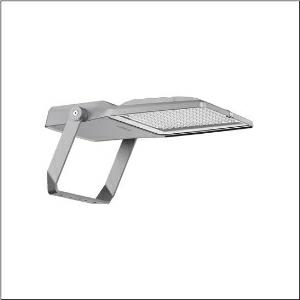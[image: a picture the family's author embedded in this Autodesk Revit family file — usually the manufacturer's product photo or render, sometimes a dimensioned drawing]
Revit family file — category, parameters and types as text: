
# Revit family: floodlight_fl_21_iq_midi___rs12_5xa7782e5b1a_e229
name_source: partatom
category: Lighting Fixtures
units: mm (PartAtom-declared; Revit-internal decimal feet)

## family parameters
Cut with Voids When Loaded = No
Host = Face
Light Source = No
Part Type = Normal
Room Calculation Point = No
Round Connector Dimension = Use Diameter
Shared = No

## types (1)
- --- (1 x LED, 24940 lm, 208.1 W, 4000K)
    Apparent Load = 208 VA
    CIE Flux Codes = 79 92 99 100 100
    Color Rendering = 80
    Color Temperature = 4000K
    Default Elevation = 1800 mm
    Description = Floodlight FL 21 iQ midi, floodlight, primary light control with lens, of PMMA, primary optical cover: protective disc, of toughened safety glass, transparent, light distribution: RS12, light emission: direct distribution, installation type: surface-mounted, lamps: LED, High Power LED, rated values: 24.940lm | 208,1W | 119,8lm/W (begin service life); end service life: 24.940lm | 227,1W; at 50% lumin. flux: 12.470lm | 90,1W | 138,4lm/W, colour temperature: 4000K, colour rendering: CRI > 80, light colour: 840, light setting 1 begin service life: 100% | 24.940lm | 208,1W | 119,8lm/W | 4.000K, light setting 1 end service life: 227,1W, further light settings possible, control: optimised constant luminous flux control (CLO 2.0), Desk-Remote (wireless, voltage-free reading and setting of iQ features in the workshop via application-optimized NFC function/RFID function), Smart-Wire, Night-Set, Temp-Guard, Street-Remote, Auto-Match, pre-setting: linear dimming characteristic, with terminal, 6-pole, mains connection: 220..240V, AC, 50/60Hz, luminaire housing, of diecast aluminium, powder-coated, SITECO metallic grey (DB 702S), corrosivity category C5 mid according to DIN EN ISO 12944suitable for swimming poolschlorine-resistant, sealing non-destructively replaceable, mounting bracket, of steel, galvanised, powder-coated, SITECO metallic grey (DB 702S), protection rating (complete): IP66, insulation class (complete): insulation class II (safety insulation), certification: CE, ENEC, VDE, protection symbol: D, impact resistance: IK08, permissible operating ambient temperature: -40..+40°C, permissible operating ambient temperature for outdoor applications: -40..+50°C, standard: DIN EN 12944, LABS conformity tested according to VDMA 24364:2018-05, packaging unit: 1 piece

Light Distribution: RS12
    Height = 76 mm
    Lamp = 1 x LED
    Lamp Light Flux = 24940 lm
    Lamp Power = 208.1 W
    Lamp count = 1
    Length = 657 mm
    Luminous efficacy = 120 lm/W
    Manufacturer = Siteco
    ModVariant = No
    Model = 5XA7782E5B1A
    Number of Poles = 1
    OnlyDefault = Yes
    Power Factor = 1
    Product Name = Floodlight FL 21 iQ midi | RS12
    Product group = floodlight | pylon annexe
    ProductGroupID = 6201
    Protection Class = Protection class II
    Protection Degree = IP 66
    RLX_Detail_Level = 1
    RLX_Emergency_Light_Flux = 0 lm
    RLX_Emergency_Type = 0
    RLX_Emergency_Type_DB = No
    RlxData = <blob elided: 141149 chars, md5=d343e325>
    Socket = socket
    Standby Power = 0 W
    System Light Flux = 24940 lm
    System Power = 208 W
    Type Comments = factory setting: luminous flux: 100 % | dim-lin: 254 | 710 mA
    Type Image = l_1006876.jpg
    URL = http://relux.com
    VarID = @adj_107649
    Voltage = 0 V
    Weight = 0.00 kg
    Width = 442 mm

## geometry (parser evidence)
native form markers: Blend x4, Sweep x11
no freeform markers — native parametric forms only
